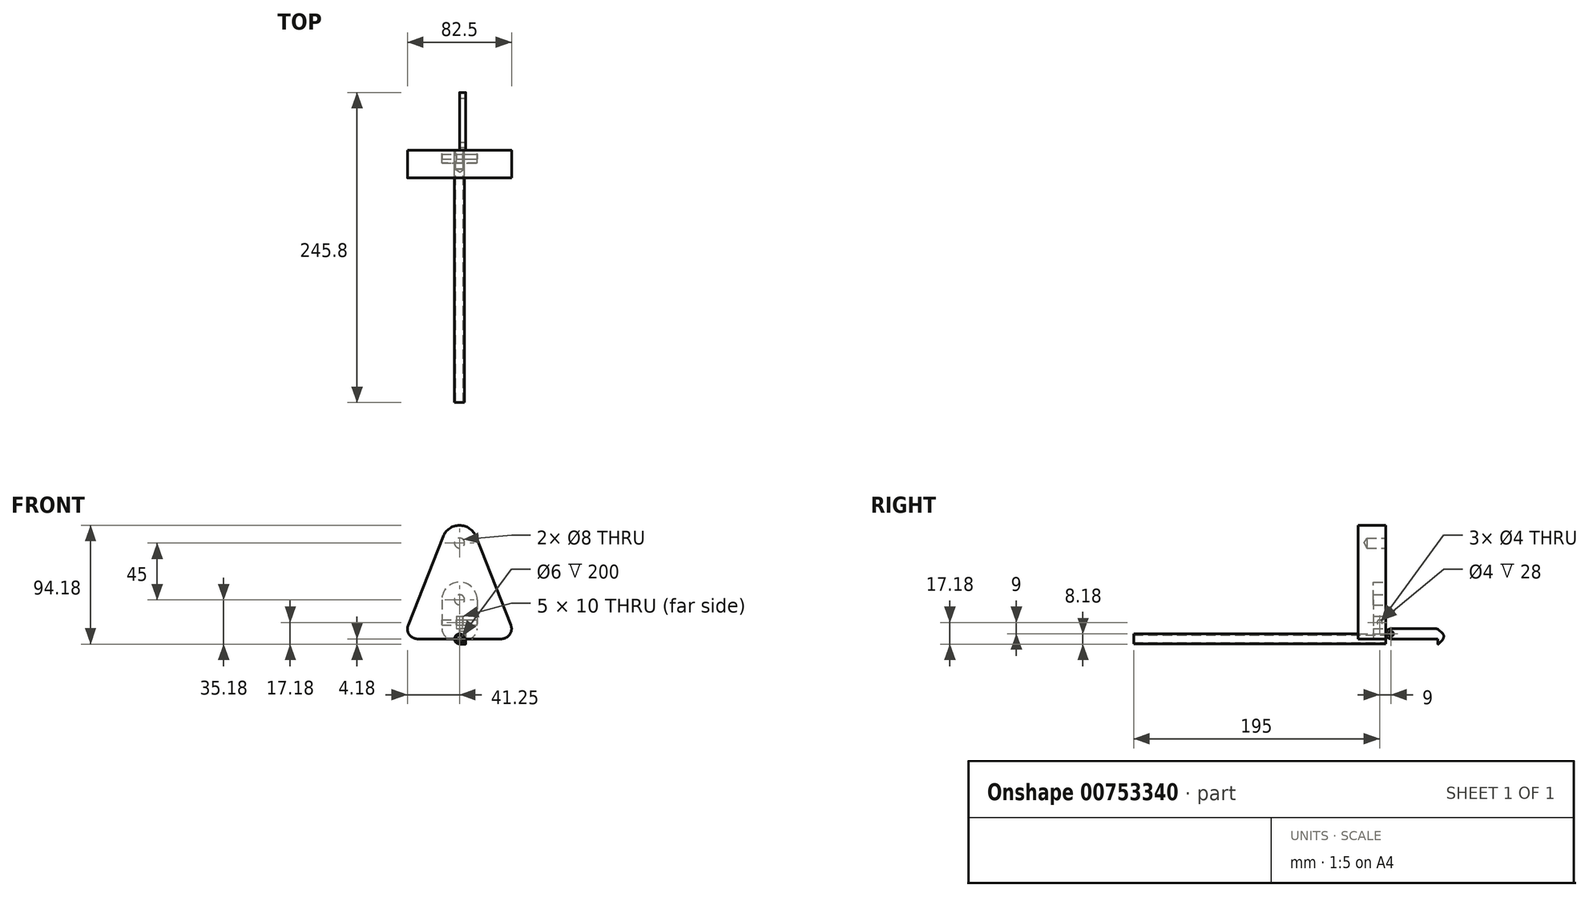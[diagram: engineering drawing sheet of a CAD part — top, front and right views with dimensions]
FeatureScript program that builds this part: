
annotation { "Feature Type Name" : "Feature", "Feature Type Description" : "" }
export const myFeature = defineFeature(function(context is Context, id is Id, definition is map)
    precondition{}
    {
        {
            var Q0;
            Q0=qCreatedBy(makeId("Front.planeOp"),FACE);
            var sketch = newSketch(context, id + "F0", { "sketchPlane" : qUnion([Q0])});
            skLineSegment(sketch, "E0", {"start": v(-45, 0) * mm, "end": v(-13.02, 81.13) * mm});
            skArc(sketch, "E1", {"start": v(13.02, 81.13) * mm, "mid": v(0, 90) * mm, "end": v(-13.02, 81.13) * mm});
            skLineSegment(sketch, "E2", {"start": v(13.02, 81.13) * mm, "end": v(45, 0) * mm});
            skLineSegment(sketch, "E3", {"start": v(-45, 0) * mm, "end": v(45, 0) * mm});
            skSolve(sketch);
        }
        {
            var Q0;
            Q0 = qSketchRegion(id + "F0", true);
            extrude(context, id + "F1", {"entities" : qUnion([Q0]), "depth" : 22 * mm, "offsetDistance" : 25 * mm});
        }
        {
            var Q0;
            Q0=makeQuery(id+"F1.opExtrude","SWEPT_EDGE",EDGE,{"disambiguationData":[OSD([sQuery(id+"F0.wireOp",EDGE,"E0"),sQuery(id+"F0.wireOp",EDGE,"E3")])]});
            var Q1;
            Q1=makeQuery(id+"F1.opExtrude","SWEPT_EDGE",EDGE,{"disambiguationData":[OSD([sQuery(id+"F0.wireOp",EDGE,"E2"),sQuery(id+"F0.wireOp",EDGE,"E3")])]});
            fillet(context, id + "F2", {"entities" : qUnion([Q0, Q1]), "radius" : 8 * mm, "tangentPropagation" : true, "allowEdgeOverflow" : false});
        }
        {
            var Q0;
            Q0=sQuery(id+"F0.wireOp",VERTEX,"E1.center");
            var Q1;
            Q1=makeQuery(id+"F1.opExtrude","SWEPT_BODY",BODY,{"disambiguationData":[OSD([sQuery(id+"F0.wireOp",EDGE,"E0"),sQuery(id+"F0.wireOp",EDGE,"E1"),sQuery(id+"F0.wireOp",EDGE,"E2"),sQuery(id+"F0.wireOp",EDGE,"E3")])]});
            hole(context, id + "F3", {"style" : HoleStyle.SIMPLE, "endStyle" : HoleEndStyle.BLIND, "oppositeDirection" : true, "standardTappedOrClearance" : lookupTablePath({ "standard" : "ISO", "size" : "8", "type" : "Drilled" }), "standardBlindInLast" : lookupTablePath({ "standard" : "ISO", "size" : "8", "type" : "Drilled" }), "holeDiameter" : 8 * mm, "majorDiameter" : 6 * mm, "holeDepth" : 15 * mm, "isTappedThrough" : true, "tappedDepth" : 12 * mm, "tapClearance" : 3, "startFromSketch" : true, "locations" : qUnion([Q0]), "scope" : qUnion([Q1])});
        }
        {
            var Q0;
            Q0=qCreatedBy(makeId("Front.planeOp"),FACE);
            var sketch = newSketch(context, id + "F4", { "sketchPlane" : qUnion([Q0])});
            skCircle(sketch, "E4", {"center": v(0, 0) * mm, "radius": 4 * mm});
            skCircle(sketch, "E5", {"center": v(0, 0) * mm, "radius": 3 * mm});
            skSolve(sketch);
        }
        {
            var Q0;
            Q0 = qSketchRegion(id + "F4", true);
            extrude(context, id + "F5", {"entities" : qUnion([Q0]), "depth" : 200 * mm, "offsetDistance" : 25 * mm});
        }
        {
            var Q0;
            Q0=qCreatedBy(makeId("Front.planeOp"),FACE);
            var sketch = newSketch(context, id + "F6", { "sketchPlane" : qUnion([Q0])});
            skCircle(sketch, "E6", {"center": v(0, 31) * mm, "radius": 14 * mm});
            skLineSegment(sketch, "E7.bottom", {"start": v(-14, 31) * mm, "end": v(14, 31) * mm});
            skLineSegment(sketch, "E7.top", {"start": v(-14, 0) * mm, "end": v(14, 0) * mm});
            skLineSegment(sketch, "E7.left", {"start": v(-14, 31) * mm, "end": v(-14, 0) * mm});
            skLineSegment(sketch, "E7.right", {"start": v(14, 31) * mm, "end": v(14, 0) * mm});
            skCircle(sketch, "E8", {"center": v(0, 31) * mm, "radius": 4 * mm});
            skLineSegment(sketch, "E9.bottom", {"start": v(-2.5, 18) * mm, "end": v(2.5, 18) * mm});
            skLineSegment(sketch, "E9.top", {"start": v(-2.5, 8) * mm, "end": v(2.5, 8) * mm});
            skLineSegment(sketch, "E9.left", {"start": v(-2.5, 18) * mm, "end": v(-2.5, 8) * mm});
            skLineSegment(sketch, "E9.right", {"start": v(2.5, 18) * mm, "end": v(2.5, 8) * mm});
            skPoint(sketch, "E9.middle", {"position": v(0, 13) * mm});
            skSolve(sketch);
        }
        {
            var Q0;
            Q0 = qSketchRegion(id + "F6", true);
            extrude(context, id + "F7", {"entities" : qUnion([Q0]), "depth" : 10 * mm, "offsetDistance" : 25 * mm});
        }
        {
            var Q0;
            Q0=makeQuery(id+"F7.opExtrude","SWEPT_EDGE",EDGE,{"disambiguationData":[OSD([sQuery(id+"F6.wireOp",EDGE,"E7.top"),sQuery(id+"F6.wireOp",EDGE,"E7.right")])]});
            var Q1;
            Q1=makeQuery(id+"F7.opExtrude","SWEPT_EDGE",EDGE,{"disambiguationData":[OSD([sQuery(id+"F6.wireOp",EDGE,"E7.top"),sQuery(id+"F6.wireOp",EDGE,"E7.left")])]});
            fillet(context, id + "F8", {"entities" : qUnion([Q0, Q1]), "radius" : 8 * mm, "tangentPropagation" : true, "allowEdgeOverflow" : false});
        }
        {
            var Q0;
            Q0=makeQuery(id+"F7.opExtrude","SWEPT_FACE",FACE,{"disambiguationData":[OSD([sQuery(id+"F6.wireOp",EDGE,"E7.right")])]});
            var sketch = newSketch(context, id + "F9", { "sketchPlane" : qUnion([Q0])});
            skLineSegment(sketch, "E10.0", {"start": v(-10, 8) * mm, "end": v(0, 8) * mm});
            skLineSegment(sketch, "E11.0", {"start": v(-10, 18) * mm, "end": v(-10, 8) * mm});
            skCircle(sketch, "E12", {"center": v(-5, 13) * mm, "radius": 2 * mm});
            skPoint(sketch, "E12.centerSnap0", {"position": v(-10, 13) * mm});
            skPoint(sketch, "E12.centerSnap1", {"position": v(-5, 8) * mm});
            skSolve(sketch);
        }
        {
            var Q0;
            Q0=makeQuery(id+"F9.imprint","IMPRINT",FACE,{"disambiguationData":[TD([[makeQuery(id+"F9.imprint","IMPRINT",EDGE,{"derivedFrom":sQuery(id+"F9.wireOp",EDGE,"E12")}),1.0]])]});
            var Q1;
            Q1=makeQuery(id+"F7.opExtrude","SWEPT_FACE",FACE,{"disambiguationData":[OSD([sQuery(id+"F6.wireOp",EDGE,"E7.left")])]});
            extrude(context, id + "F10", {"entities" : qUnion([Q0]), "operationType" : NewBodyOperationType.REMOVE, "endBound" : BoundingType.UP_TO_SURFACE, "oppositeDirection" : true, "depth" : 25 * mm, "endBoundEntityFace" : qUnion([Q1]), "offsetDistance" : 25 * mm});
        }
        {
            var Q0;
            Q0=qCreatedBy(makeId("Right.planeOp"),FACE);
            var sketch = newSketch(context, id + "F11", { "sketchPlane" : qUnion([Q0])});
            skLineSegment(sketch, "E13.bottom", {"start": v(0, 0) * mm, "end": v(41, 0) * mm});
            skLineSegment(sketch, "E13.top", {"start": v(0, 8) * mm, "end": v(41, 8) * mm});
            skLineSegment(sketch, "E13.left", {"start": v(0, 0) * mm, "end": v(0, 8) * mm});
            skLineSegment(sketch, "E13.right", {"start": v(41, 0) * mm, "end": v(41, 8) * mm});
            skLineSegment(sketch, "E14", {"start": v(41, 0) * mm, "end": v(41, -5) * mm});
            skLineSegment(sketch, "E15", {"start": v(41, -5) * mm, "end": v(47.45, 2.32) * mm});
            skLineSegment(sketch, "E16", {"start": v(47.45, 2.32) * mm, "end": v(41, 8) * mm});
            skCircle(sketch, "E17", {"center": v(4, 4) * mm, "radius": 2 * mm});
            skPoint(sketch, "E17.centerSnap0", {"position": v(0, 4) * mm});
            skSolve(sketch);
        }
        {
            var Q0;
            Q0 = qSketchRegion(id + "F11", true);
            extrude(context, id + "F12", {"entities" : qUnion([Q0]), "depth" : 5 * mm, "offsetDistance" : 25 * mm});
        }
        {
            var Q0;
            Q0=makeQuery(id+"F12.opExtrude","SWEPT_EDGE",EDGE,{"disambiguationData":[OSD([sQuery(id+"F11.wireOp",EDGE,"E13.top"),sQuery(id+"F11.wireOp",EDGE,"E13.right"),sQuery(id+"F11.wireOp",EDGE,"E16")])]});
            var Q1;
            Q1=makeQuery(id+"F12.opExtrude","SWEPT_EDGE",EDGE,{"disambiguationData":[OSD([sQuery(id+"F11.wireOp",EDGE,"E15"),sQuery(id+"F11.wireOp",EDGE,"E16")])]});
            var Q2;
            Q2=makeQuery(id+"F12.opExtrude","SWEPT_EDGE",EDGE,{"disambiguationData":[OSD([sQuery(id+"F11.wireOp",EDGE,"E13.top"),sQuery(id+"F11.wireOp",EDGE,"E13.left")])]});
            var Q3;
            Q3=makeQuery(id+"F12.opExtrude","SWEPT_EDGE",EDGE,{"disambiguationData":[OSD([sQuery(id+"F11.wireOp",EDGE,"E13.bottom"),sQuery(id+"F11.wireOp",EDGE,"E13.left")])]});
            fillet(context, id + "F13", {"entities" : qUnion([Q0, Q1, Q2, Q3]), "radius" : 4 * mm, "tangentPropagation" : true, "allowEdgeOverflow" : false});
        }
        {
            var Q0;
            Q0=makeQuery(id+"F12.opExtrude","SWEPT_EDGE",EDGE,{"disambiguationData":[OSD([sQuery(id+"F11.wireOp",EDGE,"E14"),sQuery(id+"F11.wireOp",EDGE,"E15")])]});
            fillet(context, id + "F14", {"entities" : qUnion([Q0]), "radius" : 0.5 * mm, "tangentPropagation" : true, "allowEdgeOverflow" : false});
        }
    });
